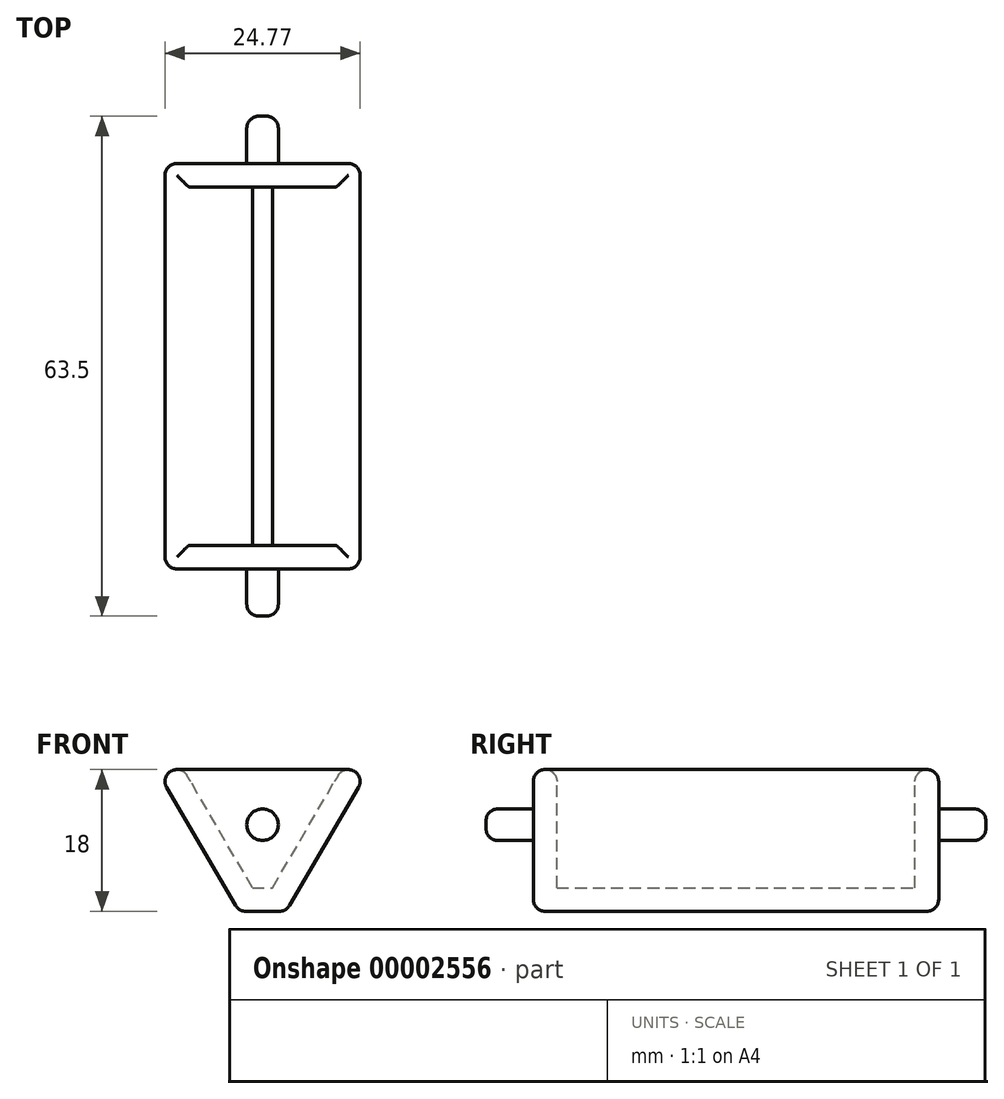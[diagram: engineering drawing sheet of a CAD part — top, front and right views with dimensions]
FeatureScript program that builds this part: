
annotation { "Feature Type Name" : "Feature", "Feature Type Description" : "" }
export const myFeature = defineFeature(function(context is Context, id is Id, definition is map)
    precondition{}
    {
        {
            var Q0;
            Q0=qCreatedBy(makeId("Front.planeOp"),FACE);
            var sketch = newSketch(context, id + "F0", { "sketchPlane" : qUnion([Q0])});
            skLineSegment(sketch, "E0", {"start": v(-8.45, 37.58) * mm, "end": v(18.55, 37.58) * mm});
            skLineSegment(sketch, "E1", {"start": v(5.05, 37.58) * mm, "end": v(5.05, 19.58) * mm, "construction": true});
            skLineSegment(sketch, "E2", {"start": v(5.05, 19.58) * mm, "end": v(8.05, 19.58) * mm});
            skLineSegment(sketch, "E3.0.MirrorCS", {"start": v(5.05, 19.58) * mm, "end": v(2.05, 19.58) * mm});
            skLineSegment(sketch, "E4", {"start": v(8.05, 19.58) * mm, "end": v(18.55, 37.58) * mm});
            skLineSegment(sketch, "E5", {"start": v(2.05, 19.58) * mm, "end": v(-8.45, 37.58) * mm});
            skSolve(sketch);
        }
        {
            var Q0;
            Q0=makeQuery(id+"F0.imprint","IMPRINT",FACE,{"disambiguationData":[TD([[makeQuery(id+"F0.imprint","IMPRINT",EDGE,{"derivedFrom":sQuery(id+"F0.wireOp",EDGE,"E0")}),-1.0]])]});
            extrude(context, id + "F1", {"entities" : qUnion([Q0]), "depth" : 51.5 * mm});
        }
        {
            var Q0;
            Q0=makeQuery(id+"F1.opExtrude","SWEPT_FACE",FACE,{"disambiguationData":[OSD([sQuery(id+"F0.wireOp",EDGE,"E0")])]});
            shell(context, id + "F2", {"entities" : qUnion([Q0]), "thickness" : 3 * mm});
        }
        {
            var Q0;
            Q0=makeQuery(id+"F1.opExtrude","SWEPT_EDGE",EDGE,{"disambiguationData":[OSD([sQuery(id+"F0.wireOp",EDGE,"E0"),sQuery(id+"F0.wireOp",EDGE,"E4")])]});
            var Q1;
            Q1=makeQuery(id+"F1.opExtrude","CAP_EDGE",EDGE,{"disambiguationData":[OSD([sQuery(id+"F0.wireOp",EDGE,"E0")])],"isStart":false});
            var Q2;
            Q2=makeQuery(id+"F1.opExtrude","SWEPT_EDGE",EDGE,{"disambiguationData":[OSD([sQuery(id+"F0.wireOp",EDGE,"E0"),sQuery(id+"F0.wireOp",EDGE,"E5")])]});
            var Q3;
            Q3=makeQuery(id+"F1.opExtrude","CAP_EDGE",EDGE,{"disambiguationData":[OSD([sQuery(id+"F0.wireOp",EDGE,"E0")])],"isStart":true});
            var Q4;
            {var subQ0=sQuery(id+"F0.wireOp",EDGE,"E0");Q4=makeQuery(id+"F2.opShell","OFFSET_EDGE",EDGE,{"disambiguationData":[OSD([subQ0]),TDD([makeQuery(id+"F1.opExtrude","CAP_EDGE",EDGE,{"disambiguationData":[OSD([subQ0])],"isStart":false})])]});}
            var Q5;
            Q5=makeQuery(id+"F2.opShell","OFFSET_EDGE",EDGE,{"disambiguationData":[OSD([sQuery(id+"F0.wireOp",EDGE,"E0"),sQuery(id+"F0.wireOp",EDGE,"E5")])]});
            var Q6;
            {var subQ0=sQuery(id+"F0.wireOp",EDGE,"E0");Q6=makeQuery(id+"F2.opShell","OFFSET_EDGE",EDGE,{"disambiguationData":[OSD([subQ0]),TDD([makeQuery(id+"F1.opExtrude","CAP_EDGE",EDGE,{"disambiguationData":[OSD([subQ0])],"isStart":true})])]});}
            var Q7;
            Q7=makeQuery(id+"F2.opShell","OFFSET_EDGE",EDGE,{"disambiguationData":[OSD([sQuery(id+"F0.wireOp",EDGE,"E0"),sQuery(id+"F0.wireOp",EDGE,"E4")])]});
            var Q8;
            Q8=makeQuery(id+"F1.opExtrude","CAP_EDGE",EDGE,{"disambiguationData":[OSD([sQuery(id+"F0.wireOp",EDGE,"E5")])],"isStart":false});
            var Q9;
            Q9=makeQuery(id+"F1.opExtrude","CAP_EDGE",EDGE,{"disambiguationData":[OSD([sQuery(id+"F0.wireOp",EDGE,"E4")])],"isStart":false});
            var Q10;
            Q10=makeQuery(id+"F1.opExtrude","CAP_EDGE",EDGE,{"disambiguationData":[OSD([sQuery(id+"F0.wireOp",EDGE,"E3.0.MirrorCS")])],"isStart":false});
            var Q11;
            Q11=makeQuery(id+"F1.opExtrude","CAP_EDGE",EDGE,{"disambiguationData":[OSD([sQuery(id+"F0.wireOp",EDGE,"E5")])],"isStart":true});
            var Q12;
            Q12=makeQuery(id+"F1.opExtrude","CAP_EDGE",EDGE,{"disambiguationData":[OSD([sQuery(id+"F0.wireOp",EDGE,"E4")])],"isStart":true});
            var Q13;
            Q13=makeQuery(id+"F1.opExtrude","CAP_EDGE",EDGE,{"disambiguationData":[OSD([sQuery(id+"F0.wireOp",EDGE,"E3.0.MirrorCS")])],"isStart":true});
            var Q14;
            Q14=makeQuery(id+"F1.opExtrude","SWEPT_EDGE",EDGE,{"disambiguationData":[OSD([sQuery(id+"F0.wireOp",EDGE,"E3.0.MirrorCS"),sQuery(id+"F0.wireOp",EDGE,"E5")])]});
            var Q15;
            Q15=makeQuery(id+"F1.opExtrude","SWEPT_EDGE",EDGE,{"disambiguationData":[OSD([sQuery(id+"F0.wireOp",EDGE,"E3.0.MirrorCS"),sQuery(id+"F0.wireOp",EDGE,"E4")])]});
            fillet(context, id + "F3", {"entities" : qUnion([Q0, Q1, Q2, Q3, Q4, Q5, Q6, Q7, Q8, Q9, Q10, Q11, Q12, Q13, Q14, Q15]), "radius" : 1.5 * mm, "tangentPropagation" : true, "allowEdgeOverflow" : false});
        }
        {
            var Q0;
            Q0=makeQuery(id+"F1.opExtrude","CAP_FACE",FACE,{"disambiguationData":[OSD([sQuery(id+"F0.wireOp",EDGE,"E0"),sQuery(id+"F0.wireOp",EDGE,"E3.0.MirrorCS"),sQuery(id+"F0.wireOp",EDGE,"E4"),sQuery(id+"F0.wireOp",EDGE,"E5")])],"isStart":false});
            var sketch = newSketch(context, id + "F4", { "sketchPlane" : qUnion([Q0])});
            skLineSegment(sketch, "E6", {"start": v(5.05, 36.08) * mm, "end": v(5.05, 21.08) * mm, "construction": true});
            skCircle(sketch, "E7", {"center": v(5.05, 30.58) * mm, "radius": 2 * mm});
            skSolve(sketch);
        }
        {
            var Q0;
            Q0=makeQuery(id+"F4.imprint","IMPRINT",FACE,{"disambiguationData":[TD([[makeQuery(id+"F4.imprint","IMPRINT",EDGE,{"derivedFrom":sQuery(id+"F4.wireOp",EDGE,"E7")}),1.0]])]});
            var Q1;
            Q1=sQuery(id+"F4.wireOp",EDGE,"E7");
            extrude(context, id + "F5", {"entities" : qUnion([Q0]), "surfaceEntities" : qUnion([Q1]), "depth" : 6 * mm});
        }
        {
            var Q0;
            Q0=makeQuery(id+"F5.opExtrude","CAP_EDGE",EDGE,{"disambiguationData":[OSD([sQuery(id+"F4.wireOp",EDGE,"E7")])],"isStart":false});
            fillet(context, id + "F6", {"entities" : qUnion([Q0]), "radius" : 1.5 * mm, "tangentPropagation" : true, "allowEdgeOverflow" : false});
        }
        {
            var Q0;
            Q0=makeQuery(id+"F1.opExtrude","CAP_FACE",FACE,{"disambiguationData":[OSD([sQuery(id+"F0.wireOp",EDGE,"E0"),sQuery(id+"F0.wireOp",EDGE,"E3.0.MirrorCS"),sQuery(id+"F0.wireOp",EDGE,"E4"),sQuery(id+"F0.wireOp",EDGE,"E5")])],"isStart":false});
            var Q1;
            Q1=makeQuery(id+"F1.opExtrude","CAP_FACE",FACE,{"disambiguationData":[OSD([sQuery(id+"F0.wireOp",EDGE,"E0"),sQuery(id+"F0.wireOp",EDGE,"E3.0.MirrorCS"),sQuery(id+"F0.wireOp",EDGE,"E4"),sQuery(id+"F0.wireOp",EDGE,"E5")])],"isStart":true});
            cPlane(context, id + "F7", {"entities" : qUnion([Q0, Q1]), "cplaneType" : CPlaneType.MID_PLANE, "offset" : 150 * mm, "width" : 150 * mm, "height" : 150 * mm});
        }
        {
            var Q0;
            Q0=makeQuery(id+"F5.opExtrude","SWEPT_BODY",BODY,{"disambiguationData":[OSD([sQuery(id+"F4.wireOp",EDGE,"E7")])]});
            var Q1;
            Q1=qCreatedBy(id+"F7.planeOp",FACE);
            mirror(context, id + "F8", {"entities" : qUnion([Q0]), "mirrorPlane" : qUnion([Q1])});
        }
    });
